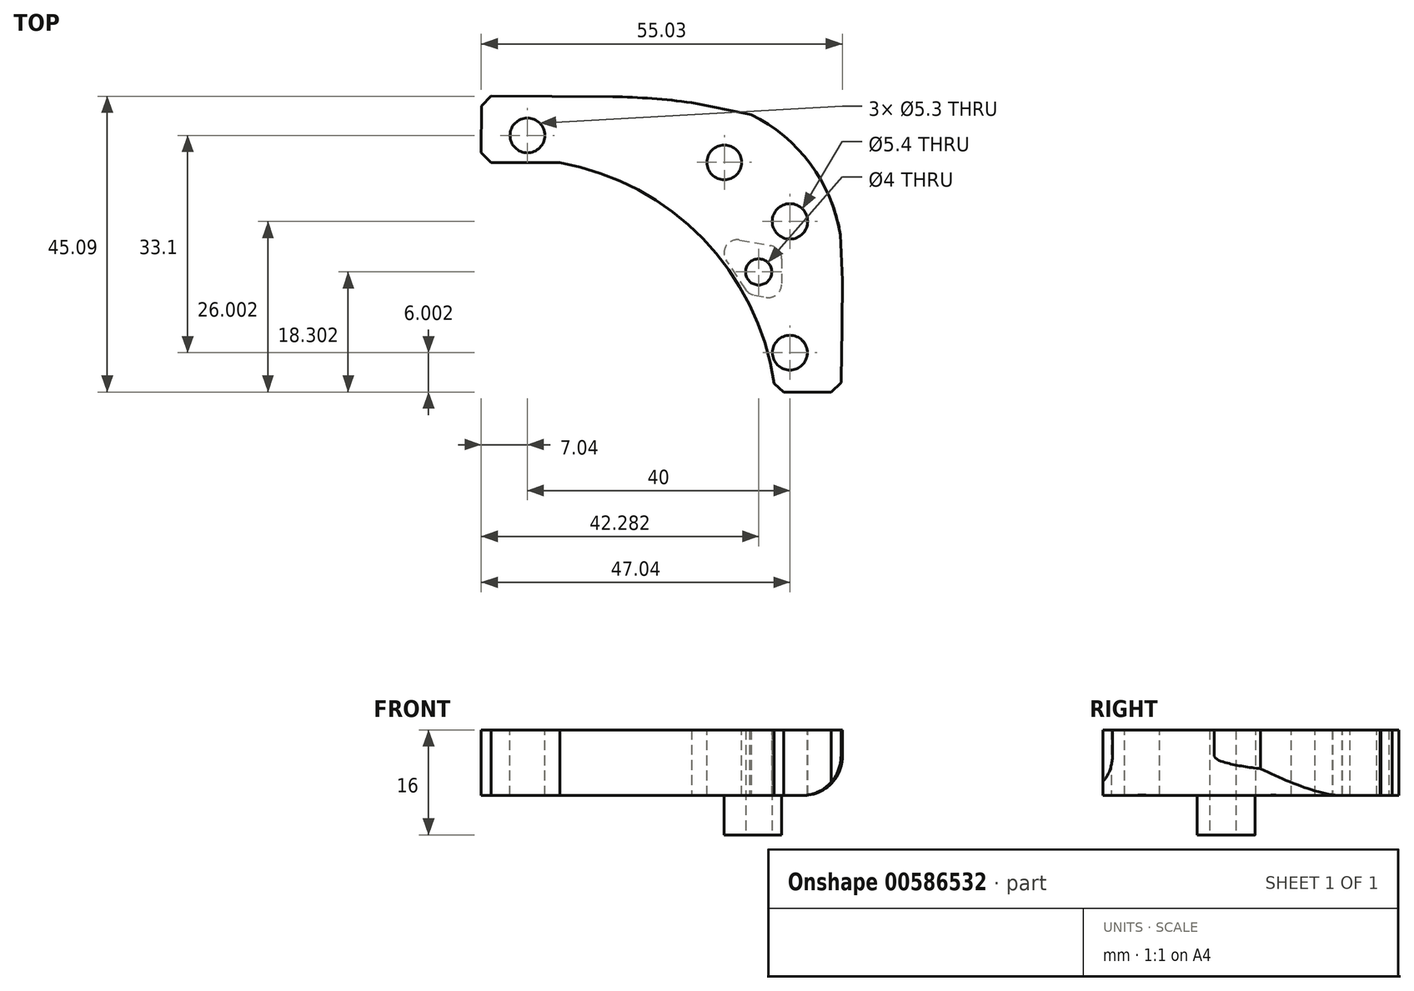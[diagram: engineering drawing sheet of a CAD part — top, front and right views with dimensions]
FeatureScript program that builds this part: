
annotation { "Feature Type Name" : "Feature", "Feature Type Description" : "" }
export const myFeature = defineFeature(function(context is Context, id is Id, definition is map)
    precondition{}
    {
        {
            var Q0;
            Q0=qCreatedBy(makeId("Top.planeOp"),FACE);
            var sketch = newSketch(context, id + "F0", { "sketchPlane" : qUnion([Q0])});
            skLineSegment(sketch, "E0", {"start": v(-54.75, -11.15) * mm, "end": v(-54.8, -21.25) * mm});
            skArc(sketch, "E1", {"start": v(-13.75, -13.92) * mm, "mid": v(-4.67, -21.42) * mm, "end": v(-0.07, -32.25) * mm});
            skLineSegment(sketch, "E2", {"start": v(-54.75, -11.15) * mm, "end": v(-34.75, -11.25) * mm});
            skArc(sketch, "E3", {"start": v(-34.75, -11.25) * mm, "mid": v(-28.74, -11.52) * mm, "end": v(-22.75, -12.15) * mm});
            skLineSegment(sketch, "E4", {"start": v(-22.75, -12.15) * mm, "end": v(-13.75, -13.92) * mm});
            skPoint(sketch, "E5.orphan", {"position": v(0.25, -36.25) * mm});
            skArc(sketch, "E6", {"start": v(0, -56.25) * mm, "mid": v(0.17, -47.75) * mm, "end": v(0.24, -39.25) * mm});
            skLineSegment(sketch, "E7", {"start": v(0, -56.25) * mm, "end": v(-10, -56.25) * mm});
            skLineSegment(sketch, "E8", {"start": v(-54.8, -21.25) * mm, "end": v(-42.8, -21.3) * mm});
            skArc(sketch, "E9", {"start": v(-10, -56.25) * mm, "mid": v(-20.59, -33.32) * mm, "end": v(-42.8, -21.3) * mm});
            skLineSegment(sketch, "E10", {"start": v(-0.07, -32.25) * mm, "end": v(0.24, -39.25) * mm});
            skSolve(sketch);
        }
        {
            var Q0;
            Q0=qSketchRegion(id+"F0",true);
            extrude(context, id + "F1", {"entities" : qUnion([Q0]), "depth" : 10 * mm});
        }
        {
            var Q0;
            Q0=makeQuery(id+"F1.opExtrude","CAP_FACE",FACE,{"disambiguationData":[OSD([sQuery(id+"F0.wireOp",EDGE,"sl27yMI0-AFCf-Kcrl-0bmQ-pZ9rT9zFnCGi"),sQuery(id+"F0.wireOp",EDGE,"BDBsffxZ-tEOx-Hil9-iUUA-GEFrlKPdEFfM"),sQuery(id+"F0.wireOp",EDGE,"E0"),sQuery(id+"F0.wireOp",EDGE,"FjBfGWs7-kI8q-3lPp-M7p8-NHLP12ySko6t"),sQuery(id+"F0.wireOp",EDGE,"xpgikVl3-DIja-vaeT-NMQl-5fUiDFNzWjIU"),sQuery(id+"F0.wireOp",EDGE,"E1"),sQuery(id+"F0.wireOp",EDGE,"15a26400-cb63-4f5f-8ce6-d631993ec03b")])],"isStart":false});
            var sketch = newSketch(context, id + "F2", { "sketchPlane" : qUnion([Q0])});
            skCircle(sketch, "E11", {"center": v(-47.75, -17.15) * mm, "radius": 2.65 * mm});
            skCircle(sketch, "E12", {"center": v(-17.75, -21.25) * mm, "radius": 2.65 * mm});
            skCircle(sketch, "E13", {"center": v(-7.75, -50.25) * mm, "radius": 2.65 * mm});
            skCircle(sketch, "E14", {"center": v(-7.75, -30.25) * mm, "radius": 2.7 * mm});
            skSolve(sketch);
        }
        {
            var Q0;
            Q0=qSketchRegion(id+"F2",true);
            extrude(context, id + "F3", {"entities" : qUnion([Q0]), "operationType" : NewBodyOperationType.REMOVE, "endBound" : BoundingType.THROUGH_ALL, "oppositeDirection" : true, "depth" : 25 * mm});
        }
        {
            var Q0;
            Q0=makeQuery(id+"F1.opExtrude","CAP_EDGE",EDGE,{"disambiguationData":[OSD([sQuery(id+"F0.wireOp",EDGE,"E6")])],"isStart":true});
            fillet(context, id + "F4", {"entities" : qUnion([Q0]), "radius" : 6 * mm, "allowEdgeOverflow" : false});
        }
        {
            var Q0;
            Q0=makeQuery(id+"F0.imprint","IMPRINT",FACE,{"disambiguationData":[TD([[makeQuery(id+"F0.imprint","IMPRINT",EDGE,{"derivedFrom":sQuery(id+"F0.wireOp",EDGE,"E0")}),1.0]])]});
            var sketch = newSketch(context, id + "F5", { "sketchPlane" : qUnion([Q0])});
            skLineSegment(sketch, "E15.bottom", {"start": v(-14.04, -41.34) * mm, "end": v(-9.04, -42.25) * mm});
            skLineSegment(sketch, "E15.left", {"start": v(-14.04, -41.34) * mm, "end": v(-20, -32.25) * mm});
            skLineSegment(sketch, "E16", {"start": v(-20, -32.25) * mm, "end": v(-9, -34.25) * mm});
            skLineSegment(sketch, "E17", {"start": v(-9, -34.25) * mm, "end": v(-9.04, -42.25) * mm});
            skSolve(sketch);
        }
        {
            var Q0;
            Q0=makeQuery(id+"F5.imprint","IMPRINT",FACE,{"disambiguationData":[TD([[makeQuery(id+"F5.imprint","IMPRINT",EDGE,{"derivedFrom":sQuery(id+"F5.wireOp",EDGE,"E15.bottom")}),1.0]])]});
            extrude(context, id + "F6", {"entities" : qUnion([Q0]), "operationType" : NewBodyOperationType.ADD, "oppositeDirection" : true, "depth" : 6 * mm, "offsetDistance" : 25 * mm});
        }
        {
            var Q0;
            Q0=makeQuery(id+"F6.opExtrude","SWEPT_EDGE",EDGE,{"disambiguationData":[OSD([sQuery(id+"F5.wireOp",EDGE,"E15.top"),sQuery(id+"F5.wireOp",EDGE,"E15.left")])]});
            var Q1;
            Q1=makeQuery(id+"F6.opExtrude","SWEPT_EDGE",EDGE,{"disambiguationData":[OSD([sQuery(id+"F5.wireOp",EDGE,"E15.top"),sQuery(id+"F5.wireOp",EDGE,"E15.right")])]});
            var Q2;
            Q2=makeQuery(id+"F6.opExtrude","SWEPT_EDGE",EDGE,{"disambiguationData":[OSD([sQuery(id+"F5.wireOp",EDGE,"E15.bottom"),sQuery(id+"F5.wireOp",EDGE,"E15.right")])]});
            var Q3;
            Q3=makeQuery(id+"F6.opExtrude","SWEPT_EDGE",EDGE,{"disambiguationData":[OSD([sQuery(id+"F5.wireOp",EDGE,"E16"),sQuery(id+"F5.wireOp",EDGE,"E17")])]});
            fillet(context, id + "F7", {"entities" : qUnion([Q0, Q1, Q2, Q3]), "radius" : 2 * mm, "tangentPropagation" : true, "allowEdgeOverflow" : false});
        }
        {
            var Q0;
            Q0=makeQuery(id+"F1.opExtrude","SWEPT_EDGE",EDGE,{"disambiguationData":[OSD([sQuery(id+"F0.wireOp",EDGE,"E0"),sQuery(id+"F0.wireOp",EDGE,"E2")])]});
            var Q1;
            Q1=makeQuery(id+"F1.opExtrude","SWEPT_EDGE",EDGE,{"disambiguationData":[OSD([sQuery(id+"F0.wireOp",EDGE,"E0"),sQuery(id+"F0.wireOp",EDGE,"E8")])]});
            var Q2;
            Q2=makeQuery(id+"F1.opExtrude","SWEPT_EDGE",EDGE,{"disambiguationData":[OSD([sQuery(id+"F0.wireOp",EDGE,"E7"),sQuery(id+"F0.wireOp",EDGE,"E9")])]});
            var Q3;
            Q3=makeQuery(id+"F1.opExtrude","SWEPT_EDGE",EDGE,{"disambiguationData":[OSD([sQuery(id+"F0.wireOp",EDGE,"E6"),sQuery(id+"F0.wireOp",EDGE,"E7")])]});
            chamfer(context, id + "F8", {"entities" : qUnion([Q0, Q1, Q2, Q3]), "width" : 1.5 * mm});
        }
        {
            var Q0;
            Q0=makeQuery(id+"F1.opExtrude","SWEPT_EDGE",EDGE,{"disambiguationData":[OSD([sQuery(id+"F0.wireOp",EDGE,"E1"),sQuery(id+"F0.wireOp",EDGE,"E4")])]});
            chamfer(context, id + "F9", {"entities" : qUnion([Q0]), "width" : 1 * mm, "tangentPropagation" : true});
        }
        {
            var Q0;
            Q0=makeQuery(id+"F6.opExtrude","CAP_FACE",FACE,{"disambiguationData":[OSD([sQuery(id+"F5.wireOp",EDGE,"E15.bottom"),sQuery(id+"F5.wireOp",EDGE,"E15.left"),sQuery(id+"F5.wireOp",EDGE,"E16"),sQuery(id+"F5.wireOp",EDGE,"E17")])],"isStart":false});
            var sketch = newSketch(context, id + "F10", { "sketchPlane" : qUnion([Q0])});
            skCircle(sketch, "E18", {"center": v(-12.5, 37.95) * mm, "radius": 2 * mm});
            skSolve(sketch);
        }
        {
            var Q0;
            Q0=qSketchRegion(id+"F10",true);
            var Q1;
            Q1=makeQuery(id+"F1.opExtrude","CAP_FACE",FACE,{"disambiguationData":[OSD([sQuery(id+"F0.wireOp",EDGE,"E0"),sQuery(id+"F0.wireOp",EDGE,"E1"),sQuery(id+"F0.wireOp",EDGE,"E2"),sQuery(id+"F0.wireOp",EDGE,"E3"),sQuery(id+"F0.wireOp",EDGE,"E4"),sQuery(id+"F0.wireOp",EDGE,"E6"),sQuery(id+"F0.wireOp",EDGE,"E7"),sQuery(id+"F0.wireOp",EDGE,"E8"),sQuery(id+"F0.wireOp",EDGE,"E9"),sQuery(id+"F0.wireOp",EDGE,"E10")])],"isStart":false});
            extrude(context, id + "F11", {"entities" : qUnion([Q0]), "operationType" : NewBodyOperationType.REMOVE, "endBound" : BoundingType.UP_TO_SURFACE, "oppositeDirection" : true, "depth" : 25 * mm, "endBoundEntityFace" : qUnion([Q1]), "offsetDistance" : 25 * mm});
        }
    });
